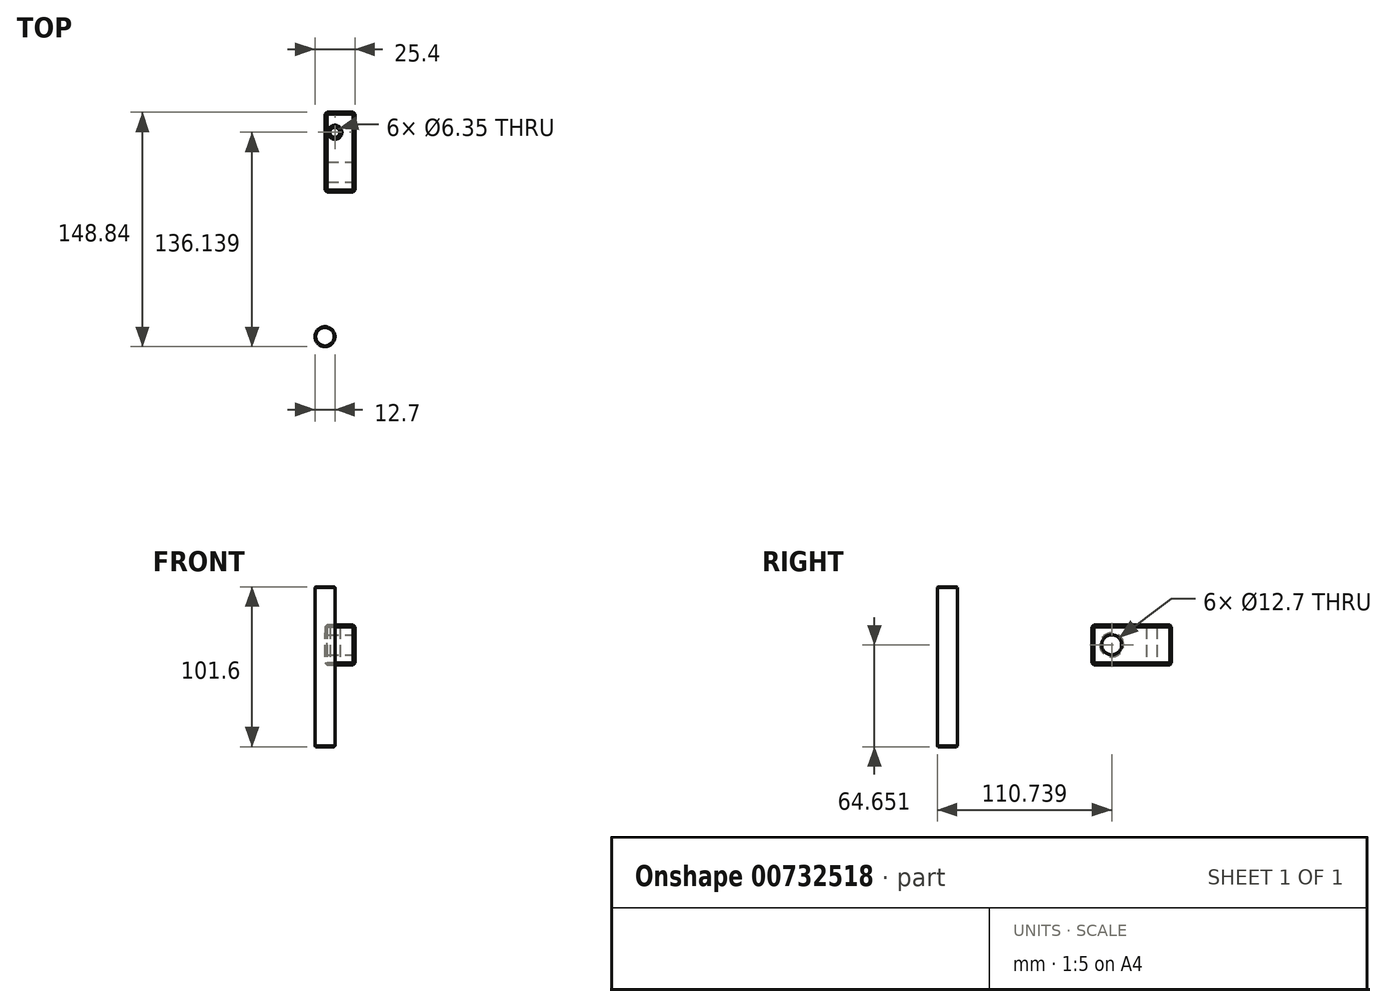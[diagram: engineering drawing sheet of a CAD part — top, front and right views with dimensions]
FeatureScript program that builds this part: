
annotation { "Feature Type Name" : "Feature", "Feature Type Description" : "" }
export const myFeature = defineFeature(function(context is Context, id is Id, definition is map)
    precondition{}
    {
        {
            var Q0;
            Q0=qCreatedBy(makeId("Top.planeOp"),FACE);
            var sketch = newSketch(context, id + "F0", { "sketchPlane" : qUnion([Q0])});
            skCircle(sketch, "E0", {"center": v(0, 0) * mm, "radius": 6.35 * mm});
            skSolve(sketch);
        }
        {
            var Q0;
            Q0=makeQuery(id+"F0.imprint","IMPRINT",FACE,{"disambiguationData":[TD([[makeQuery(id+"F0.imprint","IMPRINT",EDGE,{"derivedFrom":sQuery(id+"F0.wireOp",EDGE,"E0")}),1.0]])]});
            extrude(context, id + "F1", {"entities" : qUnion([Q0]), "depth" : 101.6 * mm, "offsetDistance" : 25.4 * mm});
        }
        {
            var Q0;
            Q0=makeQuery(id+"F1.opExtrude","CAP_EDGE",EDGE,{"disambiguationData":[OSD([sQuery(id+"F0.wireOp",EDGE,"E0")])],"isStart":false});
            var Q1;
            Q1=makeQuery(id+"F1.opExtrude","CAP_EDGE",EDGE,{"disambiguationData":[OSD([sQuery(id+"F0.wireOp",EDGE,"E0")])],"isStart":true});
            chamfer(context, id + "F2", {"entities" : qUnion([Q0, Q1]), "width" : 0.5 * mm, "tangentPropagation" : true});
        }
        {
            var Q0;
            Q0=qCreatedBy(makeId("Right.planeOp"),FACE);
            var sketch = newSketch(context, id + "F3", { "sketchPlane" : qUnion([Q0])});
            skLineSegment(sketch, "E1.bottom", {"start": v(91.69, 77.35) * mm, "end": v(142.49, 77.35) * mm});
            skLineSegment(sketch, "E1.top", {"start": v(91.69, 51.95) * mm, "end": v(142.49, 51.95) * mm});
            skLineSegment(sketch, "E1.left", {"start": v(91.69, 77.35) * mm, "end": v(91.69, 51.95) * mm});
            skLineSegment(sketch, "E1.right", {"start": v(142.49, 77.35) * mm, "end": v(142.49, 51.95) * mm});
            skSolve(sketch);
        }
        {
            var Q0;
            Q0=makeQuery(id+"F3.imprint","IMPRINT",FACE,{"disambiguationData":[TD([[makeQuery(id+"F3.imprint","IMPRINT",EDGE,{"derivedFrom":sQuery(id+"F3.wireOp",EDGE,"E1.bottom")}),-1.0]])]});
            extrude(context, id + "F4", {"entities" : qUnion([Q0]), "depth" : 19.05 * mm, "offsetDistance" : 25.4 * mm});
        }
        {
            var Q0;
            Q0=makeQuery(id+"F4.opExtrude","CAP_FACE",FACE,{"disambiguationData":[OSD([sQuery(id+"F3.wireOp",EDGE,"E1.bottom"),sQuery(id+"F3.wireOp",EDGE,"E1.top"),sQuery(id+"F3.wireOp",EDGE,"E1.left"),sQuery(id+"F3.wireOp",EDGE,"E1.right")])],"isStart":false});
            var sketch = newSketch(context, id + "F5", { "sketchPlane" : qUnion([Q0])});
            skLineSegment(sketch, "E2.0.0", {"start": v(91.69, 77.35) * mm, "end": v(91.69, 51.95) * mm});
            skLineSegment(sketch, "E2.0.1", {"start": v(91.69, 51.95) * mm, "end": v(142.49, 51.95) * mm});
            skLineSegment(sketch, "E2.0.2", {"start": v(142.49, 51.95) * mm, "end": v(142.49, 77.35) * mm});
            skLineSegment(sketch, "E2.0.3", {"start": v(142.49, 77.35) * mm, "end": v(91.69, 77.35) * mm});
            skPoint(sketch, "E3", {"position": v(104.39, 64.65) * mm});
            skCircle(sketch, "E4", {"center": v(104.39, 64.65) * mm, "radius": 6.35 * mm});
            skSolve(sketch);
        }
        {
            var Q0;
            Q0=makeQuery(id+"F5.imprint","IMPRINT",FACE,{"disambiguationData":[TD([[makeQuery(id+"F5.imprint","IMPRINT",EDGE,{"derivedFrom":sQuery(id+"F5.wireOp",EDGE,"E4")}),1.0]])]});
            extrude(context, id + "F6", {"entities" : qUnion([Q0]), "operationType" : NewBodyOperationType.REMOVE, "oppositeDirection" : true, "depth" : 25.4 * mm, "offsetDistance" : 25.4 * mm});
        }
        {
            var Q0;
            Q0=makeQuery(id+"F4.opExtrude","CAP_EDGE",EDGE,{"disambiguationData":[OSD([sQuery(id+"F3.wireOp",EDGE,"E1.right")])],"isStart":false});
            var Q1;
            Q1=makeQuery(id+"F4.opExtrude","SWEPT_EDGE",EDGE,{"disambiguationData":[OSD([sQuery(id+"F3.wireOp",EDGE,"E1.bottom"),sQuery(id+"F3.wireOp",EDGE,"E1.right")])]});
            var Q2;
            Q2=makeQuery(id+"F4.opExtrude","SWEPT_EDGE",EDGE,{"disambiguationData":[OSD([sQuery(id+"F3.wireOp",EDGE,"E1.top"),sQuery(id+"F3.wireOp",EDGE,"E1.right")])]});
            var Q3;
            Q3=makeQuery(id+"F4.opExtrude","CAP_EDGE",EDGE,{"disambiguationData":[OSD([sQuery(id+"F3.wireOp",EDGE,"E1.right")])],"isStart":true});
            var Q4;
            Q4=makeQuery(id+"F4.opExtrude","CAP_EDGE",EDGE,{"disambiguationData":[OSD([sQuery(id+"F3.wireOp",EDGE,"E1.top")])],"isStart":false});
            var Q5;
            Q5=makeQuery(id+"F4.opExtrude","CAP_EDGE",EDGE,{"disambiguationData":[OSD([sQuery(id+"F3.wireOp",EDGE,"E1.bottom")])],"isStart":false});
            var Q6;
            Q6=makeQuery(id+"F4.opExtrude","CAP_EDGE",EDGE,{"disambiguationData":[OSD([sQuery(id+"F3.wireOp",EDGE,"E1.left")])],"isStart":false});
            var Q7;
            Q7=makeQuery(id+"F4.opExtrude","SWEPT_EDGE",EDGE,{"disambiguationData":[OSD([sQuery(id+"F3.wireOp",EDGE,"E1.bottom"),sQuery(id+"F3.wireOp",EDGE,"E1.left")])]});
            var Q8;
            Q8=makeQuery(id+"F4.opExtrude","SWEPT_EDGE",EDGE,{"disambiguationData":[OSD([sQuery(id+"F3.wireOp",EDGE,"E1.top"),sQuery(id+"F3.wireOp",EDGE,"E1.left")])]});
            var Q9;
            Q9=makeQuery(id+"F4.opExtrude","CAP_EDGE",EDGE,{"disambiguationData":[OSD([sQuery(id+"F3.wireOp",EDGE,"E1.left")])],"isStart":true});
            var Q10;
            Q10=makeQuery(id+"F4.opExtrude","CAP_EDGE",EDGE,{"disambiguationData":[OSD([sQuery(id+"F3.wireOp",EDGE,"E1.bottom")])],"isStart":true});
            var Q11;
            Q11=makeQuery(id+"F4.opExtrude","CAP_EDGE",EDGE,{"disambiguationData":[OSD([sQuery(id+"F3.wireOp",EDGE,"E1.top")])],"isStart":true});
            var Q12;
            Q12=makeQuery(id+"F6.boolean.opBoolean","INTERSECT",EDGE,{"derivedFrom":[makeQuery(id+"F4.opExtrude","CAP_FACE",FACE,{"disambiguationData":[OSD([sQuery(id+"F3.wireOp",EDGE,"E1.bottom"),sQuery(id+"F3.wireOp",EDGE,"E1.top"),sQuery(id+"F3.wireOp",EDGE,"E1.left"),sQuery(id+"F3.wireOp",EDGE,"E1.right")])],"isStart":true}),makeQuery(id+"F6.opExtrude","SWEPT_FACE",FACE,{"disambiguationData":[OSD([sQuery(id+"F5.wireOp",EDGE,"E4")])]})]});
            var Q13;
            Q13=makeQuery(id+"F6.boolean.opBoolean","COPY",EDGE,{"derivedFrom":makeQuery(id+"F6.opExtrude","CAP_EDGE",EDGE,{"disambiguationData":[OSD([sQuery(id+"F5.wireOp",EDGE,"E4")])],"isStart":true})});
            chamfer(context, id + "F7", {"entities" : qUnion([Q0, Q1, Q2, Q3, Q4, Q5, Q6, Q7, Q8, Q9, Q10, Q11, Q12, Q13]), "width" : 1.27 * mm, "tangentPropagation" : true});
        }
        {
            var Q0;
            Q0=makeQuery(id+"F4.opExtrude","SWEPT_FACE",FACE,{"disambiguationData":[OSD([sQuery(id+"F3.wireOp",EDGE,"E1.top")])]});
            var sketch = newSketch(context, id + "F8", { "sketchPlane" : qUnion([Q0])});
            skPoint(sketch, "E5", {"position": v(6.35, -129.79) * mm});
            skCircle(sketch, "E6", {"center": v(6.35, -129.79) * mm, "radius": 3.18 * mm});
            skSolve(sketch);
        }
        {
            var Q0;
            Q0=makeQuery(id+"F8.imprint","IMPRINT",FACE,{"disambiguationData":[TD([[makeQuery(id+"F8.imprint","IMPRINT",EDGE,{"derivedFrom":sQuery(id+"F8.wireOp",EDGE,"E6")}),1.0]])]});
            extrude(context, id + "F9", {"entities" : qUnion([Q0]), "operationType" : NewBodyOperationType.REMOVE, "oppositeDirection" : true, "depth" : 38.1 * mm, "offsetDistance" : 25.4 * mm});
        }
        {
            var Q0;
            Q0=makeQuery(id+"F9.boolean.opBoolean","COPY",EDGE,{"derivedFrom":makeQuery(id+"F9.opExtrude","CAP_EDGE",EDGE,{"disambiguationData":[OSD([sQuery(id+"F8.wireOp",EDGE,"E6")])],"isStart":true})});
            var Q1;
            Q1=makeQuery(id+"F9.boolean.opBoolean","INTERSECT",EDGE,{"derivedFrom":[makeQuery(id+"F4.opExtrude","SWEPT_FACE",FACE,{"disambiguationData":[OSD([sQuery(id+"F3.wireOp",EDGE,"E1.bottom")])]}),makeQuery(id+"F9.opExtrude","SWEPT_FACE",FACE,{"disambiguationData":[OSD([sQuery(id+"F8.wireOp",EDGE,"E6")])]})]});
            chamfer(context, id + "F10", {"entities" : qUnion([Q0, Q1]), "width" : 1.27 * mm, "tangentPropagation" : true});
        }
    });
